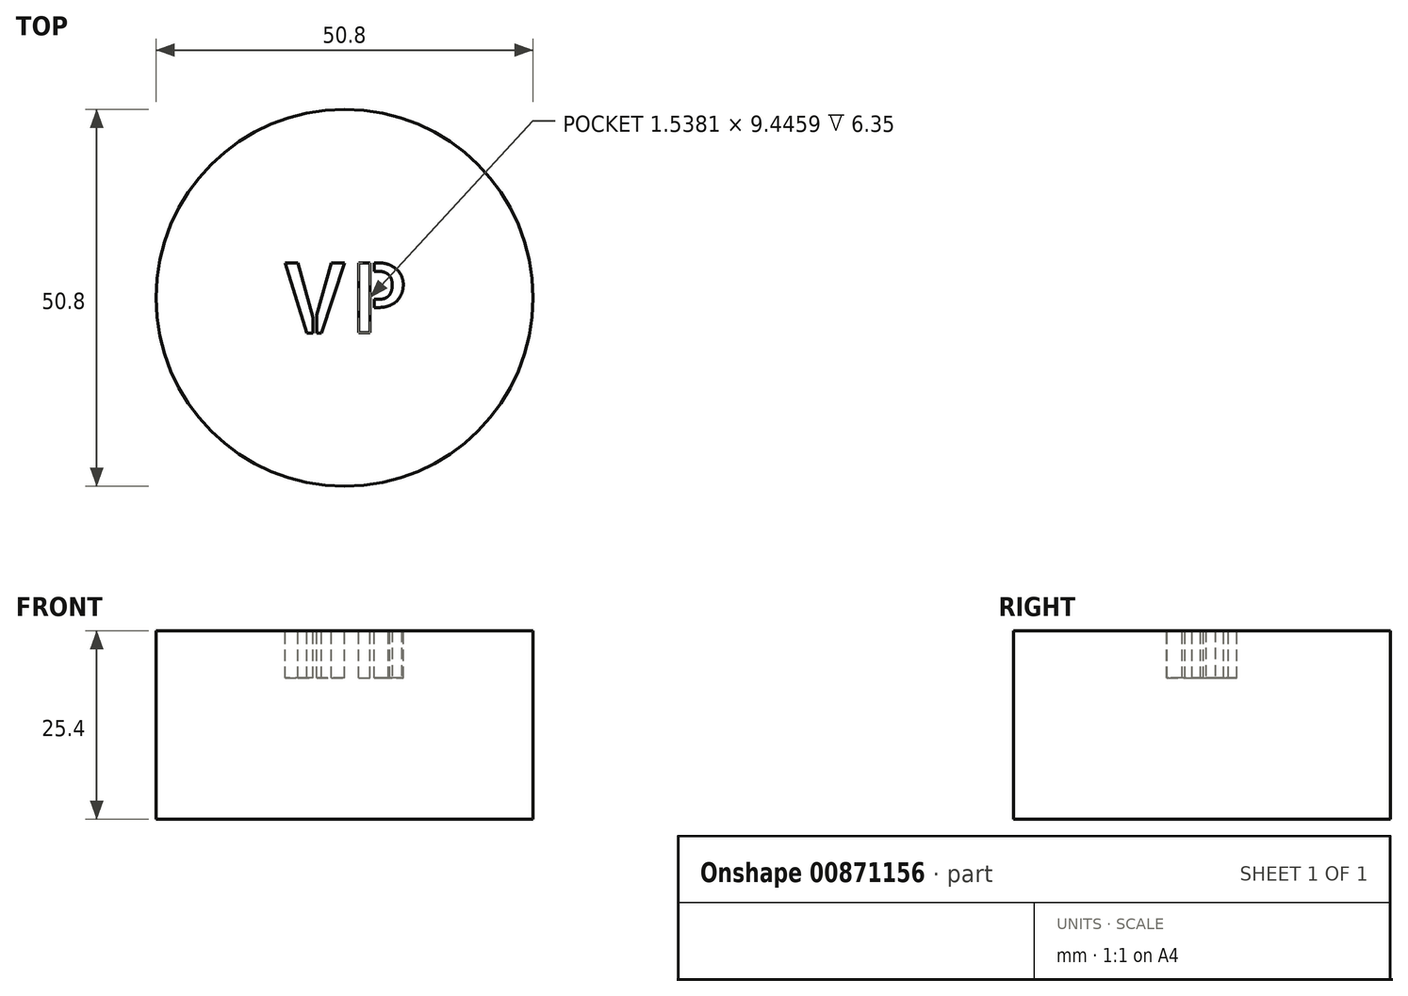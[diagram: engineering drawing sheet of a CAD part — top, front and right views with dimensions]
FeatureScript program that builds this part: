
annotation { "Feature Type Name" : "Feature", "Feature Type Description" : "" }
export const myFeature = defineFeature(function(context is Context, id is Id, definition is map)
    precondition{}
    {
        {
            var Q0;
            Q0=qCreatedBy(makeId("Top.planeOp"),FACE);
            var sketch = newSketch(context, id + "F0", { "sketchPlane" : qUnion([Q0])});
            skCircle(sketch, "E0", {"center": v(0, 0) * mm, "radius": 25.4 * mm});
            skSolve(sketch);
        }
        {
            var Q0;
            Q0 = qSketchRegion(id + "F0", true);
            extrude(context, id + "F1", {"entities" : qUnion([Q0]), "depth" : 25.4 * mm, "offsetDistance" : 25.4 * mm});
        }
        {
            var Q0;
            Q0=makeQuery(id+"F1.opExtrude","CAP_FACE",FACE,{"disambiguationData":[OSD([sQuery(id+"F0.wireOp",EDGE,"E0")])],"isStart":false});
            var sketch = newSketch(context, id + "F2", { "sketchPlane" : qUnion([Q0])});
            skText(sketch, "E1", { "text": "VP", "fontName": "AllertaStencil-Regular.ttf"});
            skLineSegment(sketch, "E2", {"start": v(-8.79, 4.72) * mm, "end": v(8.79, -4.72) * mm, "construction": true});
            skLineSegment(sketch, "E3", {"start": v(-8.79, -4.72) * mm, "end": v(8.79, 4.72) * mm, "construction": true});
            skPoint(sketch, "E4", {"position": v(0, 0) * mm});
            const initialGuessF2  = {"E1": [-0.00879, -0.00472, 1, 0, 0.00945]};
            skSetInitialGuess(sketch, initialGuessF2);
            skSolve(sketch);
        }
        {
            var Q0;
            Q0 = qSketchRegion(id + "F2", true);
            extrude(context, id + "F3", {"entities" : qUnion([Q0]), "operationType" : NewBodyOperationType.REMOVE, "oppositeDirection" : true, "depth" : 6.35 * mm, "offsetDistance" : 25.4 * mm});
        }
    });
